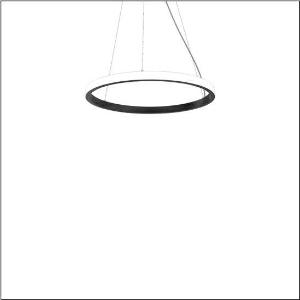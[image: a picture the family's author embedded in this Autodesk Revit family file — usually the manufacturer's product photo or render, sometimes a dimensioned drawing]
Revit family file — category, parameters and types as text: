
# Revit family: silica_r__21_ring-o_5pjbo2d1104a_b1b1
name_source: partatom
category: Lighting Fixtures
units: mm (PartAtom-declared; Revit-internal decimal feet)

## family parameters
Cut with Voids When Loaded = No
Host = Face
Light Source = No
Part Type = Normal
Room Calculation Point = No
Round Connector Dimension = Use Diameter
Shared = No

## types (1)
- Silica® 21 Ring-O (1 x LED, 4700 lm, 80 W, 3000K)
    Apparent Load = 80 VA
    CIE Flux Codes = 2 16 49 50 100
    Color Rendering = 80
    Color Temperature = 3000K
    Default Elevation = 1800 mm
    Description = Silica® 21 Ring-O, suspended luminaire, of PMMA, frosted, light emission: outer ring side luminous distribution, primary light characteristic: symmetric, installation type: suspended mounting, LED, rated luminous flux: 4.700lm, luminous efficacy: 59lm/W, light colour: 830, colour temperature: 3000K, with terminal, 5-pole, mains connection: 230V, AC/DC, 0/50..60Hz, rated input power: 80W, housing, of extruded aluminium section, jet black (RAL 9005), diameter: 810mm, ceiling canopy, jet black (RAL 9005), protection rating (lamp compartment): IP40, insulation class (complete): insulation class I (protective earthing), certification: CE, impact resistance: IK02, permissible operating ambient temperature: 0..+35°C, packaging unit: 1 piece
    Height = 48 mm  [stored 0.15748 ft]
    Lamp = 1 x LED
    Lamp Light Flux = 4700 lm
    Lamp Power = 80 W
    Lamp count = 1
    Length = 810 mm
    Luminous efficacy = 59 lm/W
    Manufacturer = Siteco
    ModVariant = No
    Model = 5PJBO2D1104A
    Mounting Place = Ceiling
    Mounting Type = Pendant
    Number of Poles = 1
    OnlyDefault = Yes
    Power Factor = 1
    Product Name = Silica® 21 Ring-O
    Product group = suspended luminaire
    ProductGroupID = 904
    Protection Class = Protection class I
    Protection Degree = Degree of protection
    RLX_Detail_Level = 1
    RLX_Emergency_Light_Flux = 0 lm
    RLX_Emergency_Type = 0
    RLX_Emergency_Type_DB = No
    RlxData = <blob elided: 14061 chars, md5=cb498286>
    Socket = socket
    Standby Power = 0 W
    System Light Flux = 4700 lm
    System Power = 80 W
    Type Comments = Product without accessories
    Type Image = l_1258381.jpg
    URL = http://relux.com
    VarID = ---
    Voltage = 0 V
    Weight = 0.00 kg
    Width = 0 mm  [stored 0 ft]

note: [stored X ft] marks values corroborated as IEEE doubles in the binary element streams (Revit-internal decimal feet)

## geometry (parser evidence)
native form markers: Sweep x13
no freeform markers — native parametric forms only
